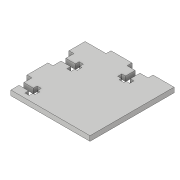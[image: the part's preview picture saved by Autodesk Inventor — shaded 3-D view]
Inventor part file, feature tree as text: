
AUTODESK INVENTOR PART (.ipt)
format: ipt  version: 2017 (Build 210142000, 142)  size: 170,496 bytes
history: native  units: in
note: dims shown in document units (in); Inventor stores cm internally (conversion verified against a paired STEP export)
features: extrude x3, sketch x3
ambient origin geometry x8: Origin, YZ Plane, XZ Plane, XY Plane, X Axis, Y Axis, Z Axis, Center Point
bodies: Solid1 (feature_tree)
feature tree (6):
  extrude  "Extrusion1"  Depth=2.0in
  extrude  "Extrusion2"  Depth=0.117in
  extrude  "Extrusion4"  Depth=0.117in
  sketch  "Sketch1"  dims[d0=2.0in d1=2.0in]
  sketch  "Sketch2"  dims[d2=0.117in d3=0.0in d4=0.117in]
  sketch  "Sketch3"  dims[d5=0.5in d6=0.117in d7=0.5in d8=0.5in d9=0.117in d10=0.5in d11=0.117in d12=0.117in d13=0.0in d14=0.0in d15=0.113in d16=0.25in d17=0.383in d18=0.289in d19=0.0in d20=0.1in d21=0.23in d22=0.23in d23=0.088in d24=0.23in d25=0.113in d26=0.053in d46=0.113in d47=0.23in d48=0.088in d49=0.088in d50=0.053in d51=0.1in d52=0.1in d60=0.1935in d61=0.0in d62=0.7874in d64=1.0in d65=0.3937in d67=1.0in d69=1.0in d70=0.0in]
